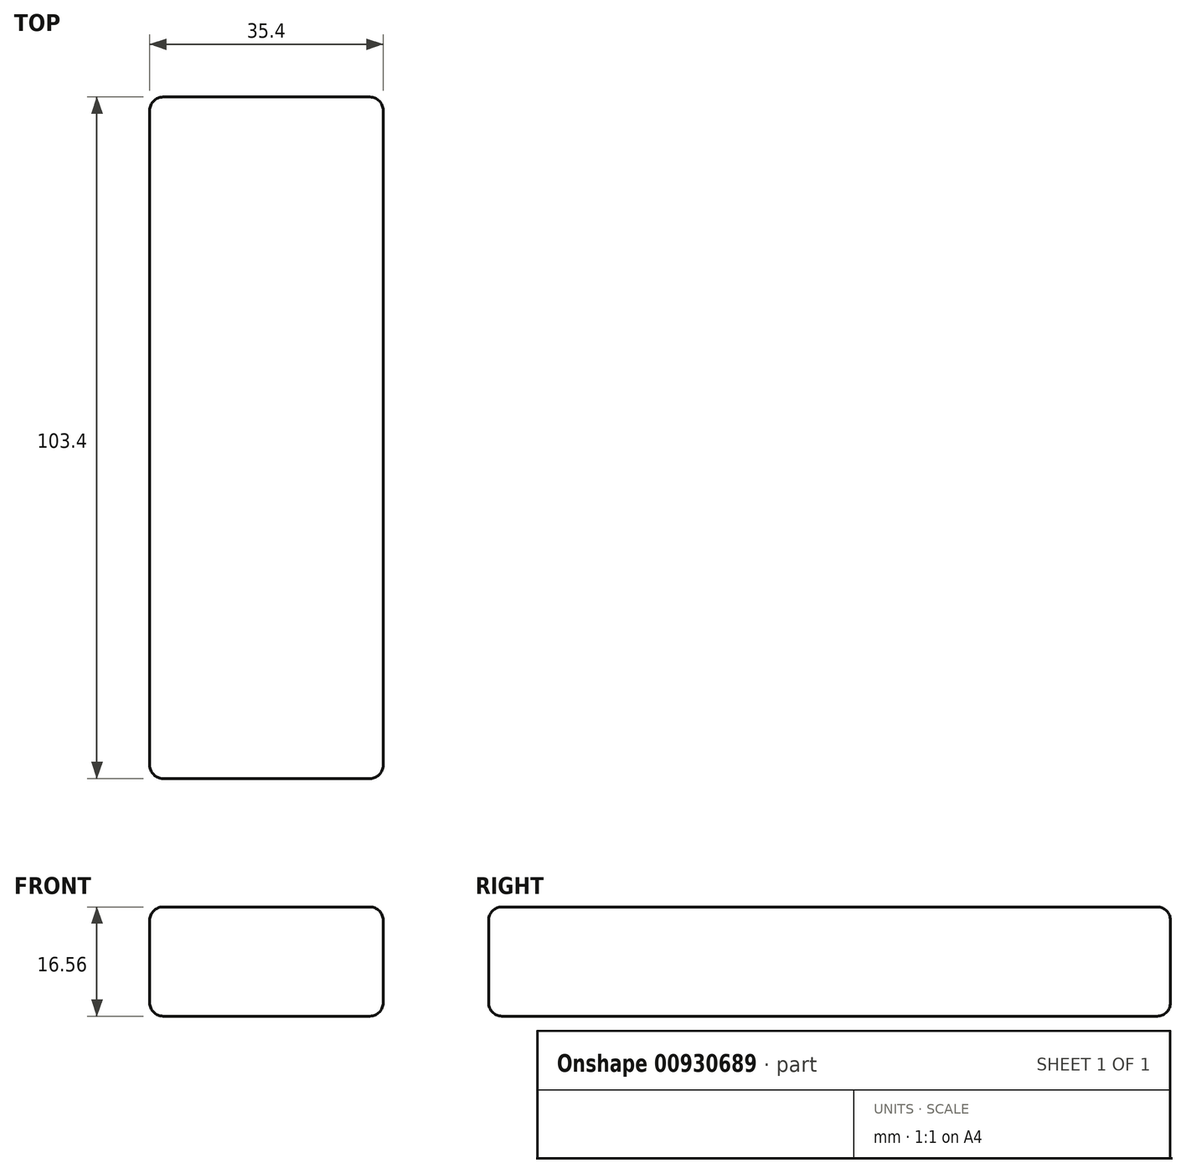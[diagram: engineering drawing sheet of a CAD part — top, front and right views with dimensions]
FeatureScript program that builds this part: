
annotation { "Feature Type Name" : "Feature", "Feature Type Description" : "" }
export const myFeature = defineFeature(function(context is Context, id is Id, definition is map)
    precondition{}
    {
        {
            var Q0;
            Q0=qCreatedBy(makeId("Front.planeOp"),FACE);
            var sketch = newSketch(context, id + "F0", { "sketchPlane" : qUnion([Q0])});
            skLineSegment(sketch, "E0.bottom", {"start": v(0, 0) * mm, "end": v(35.4, 0) * mm});
            skLineSegment(sketch, "E0.top", {"start": v(0, 16.56) * mm, "end": v(35.4, 16.56) * mm});
            skLineSegment(sketch, "E0.left", {"start": v(0, 0) * mm, "end": v(0, 16.56) * mm});
            skLineSegment(sketch, "E0.right", {"start": v(35.4, 0) * mm, "end": v(35.4, 16.56) * mm});
            skSolve(sketch);
        }
        {
            var Q0;
            Q0=qSketchRegion(id+"F0",true);
            extrude(context, id + "F1", {"entities" : qUnion([Q0]), "depth" : 103.4 * mm});
        }
        {
            var Q0;
            Q0=makeQuery(id+"F1.opExtrude","CAP_EDGE",EDGE,{"disambiguationData":[OSD([sQuery(id+"F0.wireOp",EDGE,"E0.top")])],"isStart":false});
            var Q1;
            Q1=makeQuery(id+"F1.opExtrude","CAP_EDGE",EDGE,{"disambiguationData":[OSD([sQuery(id+"F0.wireOp",EDGE,"E0.bottom")])],"isStart":false});
            var Q2;
            Q2=makeQuery(id+"F1.opExtrude","CAP_EDGE",EDGE,{"disambiguationData":[OSD([sQuery(id+"F0.wireOp",EDGE,"E0.right")])],"isStart":false});
            var Q3;
            Q3=makeQuery(id+"F1.opExtrude","CAP_EDGE",EDGE,{"disambiguationData":[OSD([sQuery(id+"F0.wireOp",EDGE,"E0.left")])],"isStart":false});
            var Q4;
            Q4=makeQuery(id+"F1.opExtrude","SWEPT_EDGE",EDGE,{"disambiguationData":[OSD([sQuery(id+"F0.wireOp",EDGE,"E0.top"),sQuery(id+"F0.wireOp",EDGE,"E0.right")])]});
            var Q5;
            Q5=makeQuery(id+"F1.opExtrude","SWEPT_EDGE",EDGE,{"disambiguationData":[OSD([sQuery(id+"F0.wireOp",EDGE,"E0.bottom"),sQuery(id+"F0.wireOp",EDGE,"E0.right")])]});
            var Q6;
            Q6=makeQuery(id+"F1.opExtrude","SWEPT_EDGE",EDGE,{"disambiguationData":[OSD([sQuery(id+"F0.wireOp",EDGE,"E0.bottom"),sQuery(id+"F0.wireOp",EDGE,"E0.left")])]});
            var Q7;
            Q7=makeQuery(id+"F1.opExtrude","SWEPT_EDGE",EDGE,{"disambiguationData":[OSD([sQuery(id+"F0.wireOp",EDGE,"E0.top"),sQuery(id+"F0.wireOp",EDGE,"E0.left")])]});
            var Q8;
            Q8=makeQuery(id+"F1.opExtrude","CAP_EDGE",EDGE,{"disambiguationData":[OSD([sQuery(id+"F0.wireOp",EDGE,"E0.bottom")])],"isStart":true});
            var Q9;
            Q9=makeQuery(id+"F1.opExtrude","CAP_EDGE",EDGE,{"disambiguationData":[OSD([sQuery(id+"F0.wireOp",EDGE,"E0.left")])],"isStart":true});
            var Q10;
            Q10=makeQuery(id+"F1.opExtrude","CAP_EDGE",EDGE,{"disambiguationData":[OSD([sQuery(id+"F0.wireOp",EDGE,"E0.top")])],"isStart":true});
            var Q11;
            Q11=makeQuery(id+"F1.opExtrude","CAP_EDGE",EDGE,{"disambiguationData":[OSD([sQuery(id+"F0.wireOp",EDGE,"E0.right")])],"isStart":true});
            fillet(context, id + "F2", {"entities" : qUnion([Q0, Q1, Q2, Q3, Q4, Q5, Q6, Q7, Q8, Q9, Q10, Q11]), "radius" : 2 * mm, "tangentPropagation" : true, "allowEdgeOverflow" : false});
        }
    });
